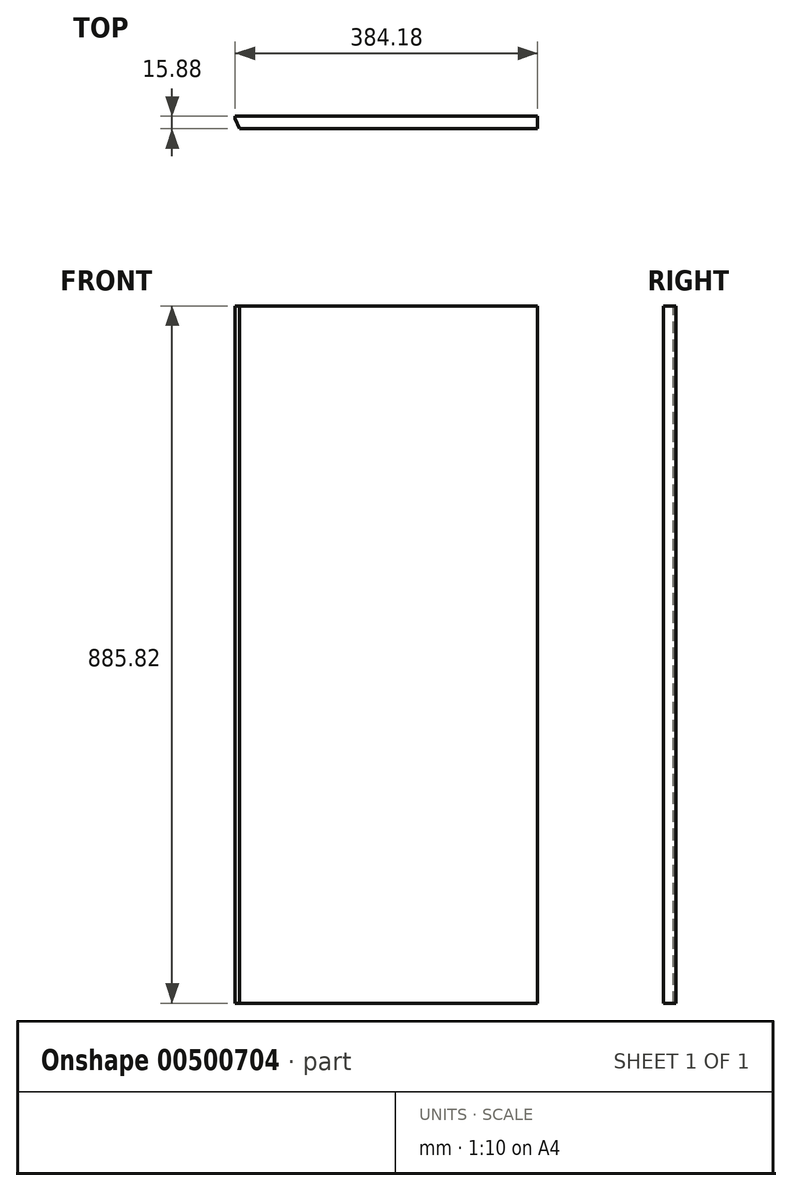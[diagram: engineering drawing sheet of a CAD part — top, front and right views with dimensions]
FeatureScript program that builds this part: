
annotation { "Feature Type Name" : "Feature", "Feature Type Description" : "" }
export const myFeature = defineFeature(function(context is Context, id is Id, definition is map)
    precondition{}
    {
        {
            var Q0;
            Q0=qCreatedBy(makeId("Front.planeOp"),FACE);
            var sketch = newSketch(context, id + "F0", { "sketchPlane" : qUnion([Q0])});
            skLineSegment(sketch, "E0.bottom", {"start": v(0, 0) * mm, "end": v(384.18, 0) * mm});
            skLineSegment(sketch, "E0.top", {"start": v(0, 885.83) * mm, "end": v(384.17, 885.83) * mm});
            skLineSegment(sketch, "E0.left", {"start": v(0, 0) * mm, "end": v(0, 885.83) * mm});
            skLineSegment(sketch, "E0.right", {"start": v(384.18, 0) * mm, "end": v(384.17, 885.83) * mm});
            skSolve(sketch);
        }
        {
            var Q0;
            Q0=makeQuery(id+"F0.imprint","IMPRINT",FACE,{"disambiguationData":[TD([[makeQuery(id+"F0.imprint","IMPRINT",EDGE,{"derivedFrom":sQuery(id+"F0.wireOp",EDGE,"E0.bottom")}),1.0]])]});
            extrude(context, id + "F1", {"entities" : qUnion([Q0]), "oppositeDirection" : true, "offsetDistance" : 25.4 * mm, "depth" : 15.88 * mm});
        }
        {
            var Q0;
            Q0=makeQuery(id+"F1.opExtrude","CAP_EDGE",EDGE,{"disambiguationData":[OSD([sQuery(id+"F0.wireOp",EDGE,"E0.left")])],"isStart":true});
            chamfer(context, id + "F2", {"entities" : qUnion([Q0]), "chamferType" : ChamferType.OFFSET_ANGLE, "width" : 12.7 * mm, "oppositeDirection" : false, "angle" : 22.5 * degree, "tangentPropagation" : true});
        }
    });
